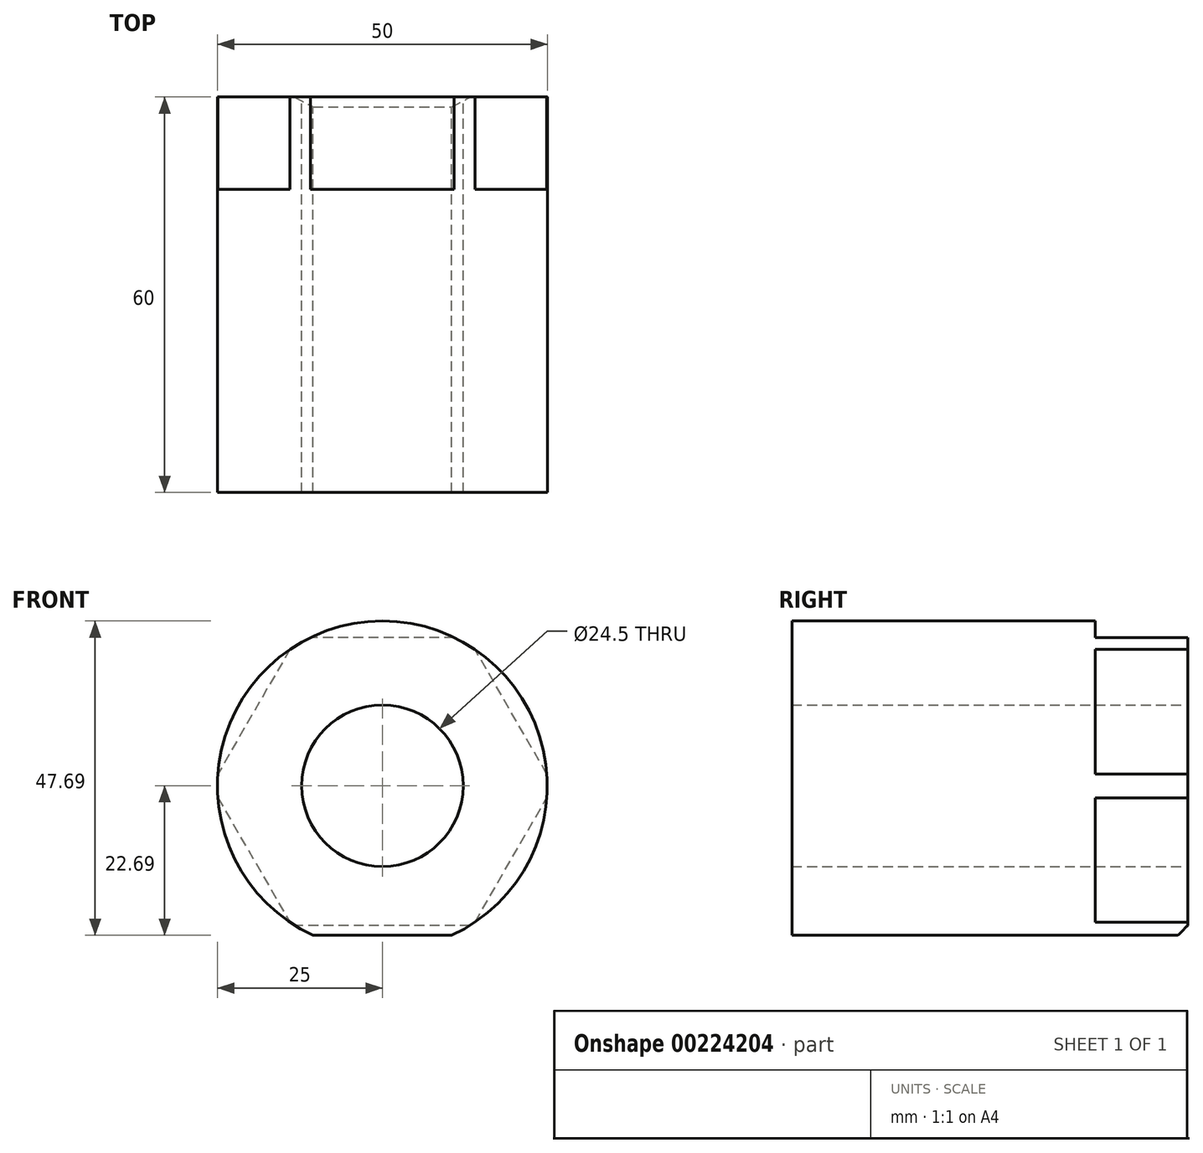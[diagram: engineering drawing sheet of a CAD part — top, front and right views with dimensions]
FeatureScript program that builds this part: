
annotation { "Feature Type Name" : "Feature", "Feature Type Description" : "" }
export const myFeature = defineFeature(function(context is Context, id is Id, definition is map)
    precondition{}
    {
        {
            var Q0;
            Q0=qCreatedBy(makeId("Front.planeOp"),FACE);
            var sketch = newSketch(context, id + "F0", { "sketchPlane" : qUnion([Q0])});
            skArc(sketch, "E0", {"start": v(10.5, -22.69) * mm, "mid": v(0, 25) * mm, "end": v(-10.5, -22.69) * mm});
            skLineSegment(sketch, "E1", {"start": v(-10.5, -22.69) * mm, "end": v(10.5, -22.69) * mm});
            skSolve(sketch);
        }
        {
            var Q0;
            Q0 = qSketchRegion(id + "F0", true);
            extrude(context, id + "F1", {"entities" : qUnion([Q0]), "depth" : 60 * mm});
        }
        {
            var Q0;
            Q0=makeQuery(id+"F1.opExtrude","CAP_FACE",FACE,{"disambiguationData":[OSD([sQuery(id+"F0.wireOp",EDGE,"E0"),sQuery(id+"F0.wireOp",EDGE,"E1")])],"isStart":true});
            var sketch = newSketch(context, id + "F2", { "sketchPlane" : qUnion([Q0])});
            skCircle(sketch, "E2.cCircle", {"center": v(0, 0) * mm, "radius": 22.5 * mm, "construction": true});
            skLineSegment(sketch, "E2.0", {"start": v(25.98, 0) * mm, "end": v(13, -22.5) * mm});
            skLineSegment(sketch, "E2.1", {"start": v(13, -22.5) * mm, "end": v(-13, -22.5) * mm});
            skLineSegment(sketch, "E2.2", {"start": v(-13, -22.5) * mm, "end": v(-25.98, 0) * mm});
            skLineSegment(sketch, "E2.3", {"start": v(-25.98, 0) * mm, "end": v(-13, 22.5) * mm});
            skLineSegment(sketch, "E2.4", {"start": v(-13, 22.5) * mm, "end": v(13, 22.5) * mm});
            skLineSegment(sketch, "E2.5", {"start": v(13, 22.5) * mm, "end": v(25.98, 0) * mm});
            skPoint(sketch, "E2.0.midPoint", {"position": v(19.49, -11.25) * mm});
            skSolve(sketch);
        }
        {
            var Q0;
            {var subQ0=sQuery(id+"F2.wireOp",EDGE,"E2.2");var subQ1=makeQuery(id+"F1.opExtrude","CAP_EDGE",EDGE,{"disambiguationData":[OSD([sQuery(id+"F0.wireOp",EDGE,"E0")])],"isStart":true});var subQ2=makeQuery(id+"F2.imprint","INTERSECT",VERTEX,{"disambiguationData":[OD(0.0)],"derivedFrom":[subQ1,subQ0]});Q0=makeQuery(id+"F2.imprint","IMPRINT",FACE,{"disambiguationData":[TD([[makeQuery(id+"F2.imprint","IMPRINT",EDGE,{"disambiguationData":[TD([[subQ2,-1.0]])],"derivedFrom":subQ0}),1.0]])]});}
            var Q1;
            {var subQ0=sQuery(id+"F2.wireOp",EDGE,"E2.3");var subQ1=makeQuery(id+"F1.opExtrude","CAP_EDGE",EDGE,{"disambiguationData":[OSD([sQuery(id+"F0.wireOp",EDGE,"E0")])],"isStart":true});var subQ2=makeQuery(id+"F2.imprint","INTERSECT",VERTEX,{"disambiguationData":[OD(0.0)],"derivedFrom":[subQ1,subQ0]});Q1=makeQuery(id+"F2.imprint","IMPRINT",FACE,{"disambiguationData":[TD([[makeQuery(id+"F2.imprint","IMPRINT",EDGE,{"disambiguationData":[TD([[subQ2,-1.0]])],"derivedFrom":subQ0}),1.0]])]});}
            var Q2;
            {var subQ0=sQuery(id+"F2.wireOp",EDGE,"E2.4");var subQ1=makeQuery(id+"F1.opExtrude","CAP_EDGE",EDGE,{"disambiguationData":[OSD([sQuery(id+"F0.wireOp",EDGE,"E0")])],"isStart":true});var subQ2=makeQuery(id+"F2.imprint","INTERSECT",VERTEX,{"disambiguationData":[OD(0.0)],"derivedFrom":[subQ1,subQ0]});Q2=makeQuery(id+"F2.imprint","IMPRINT",FACE,{"disambiguationData":[TD([[makeQuery(id+"F2.imprint","IMPRINT",EDGE,{"disambiguationData":[TD([[subQ2,-1.0]])],"derivedFrom":subQ0}),1.0]])]});}
            var Q3;
            {var subQ0=sQuery(id+"F2.wireOp",EDGE,"E2.0");var subQ1=makeQuery(id+"F1.opExtrude","CAP_EDGE",EDGE,{"disambiguationData":[OSD([sQuery(id+"F0.wireOp",EDGE,"E0")])],"isStart":true});var subQ2=makeQuery(id+"F2.imprint","INTERSECT",VERTEX,{"disambiguationData":[OD(0.0)],"derivedFrom":[subQ1,subQ0]});Q3=makeQuery(id+"F2.imprint","IMPRINT",FACE,{"disambiguationData":[TD([[makeQuery(id+"F2.imprint","IMPRINT",EDGE,{"disambiguationData":[TD([[subQ2,-1.0]])],"derivedFrom":subQ0}),1.0]])]});}
            var Q4;
            {var subQ0=sQuery(id+"F2.wireOp",EDGE,"E2.5");var subQ1=makeQuery(id+"F1.opExtrude","CAP_EDGE",EDGE,{"disambiguationData":[OSD([sQuery(id+"F0.wireOp",EDGE,"E0")])],"isStart":true});var subQ2=makeQuery(id+"F2.imprint","INTERSECT",VERTEX,{"disambiguationData":[OD(0.0)],"derivedFrom":[subQ1,subQ0]});Q4=makeQuery(id+"F2.imprint","IMPRINT",FACE,{"disambiguationData":[TD([[makeQuery(id+"F2.imprint","IMPRINT",EDGE,{"disambiguationData":[TD([[subQ2,-1.0]])],"derivedFrom":subQ0}),1.0]])]});}
            extrude(context, id + "F3", {"entities" : qUnion([Q0, Q1, Q2, Q3, Q4]), "operationType" : NewBodyOperationType.REMOVE, "oppositeDirection" : true, "depth" : 14 * mm});
        }
        {
            var Q0;
            Q0=sQuery(id+"F2.wireOp",VERTEX,"E2.cCircle.center");
            var Q1;
            Q1=makeQuery(id+"F1.opExtrude","SWEPT_BODY",BODY,{"disambiguationData":[OSD([sQuery(id+"F0.wireOp",EDGE,"E0"),sQuery(id+"F0.wireOp",EDGE,"E1")])]});
            hole(context, id + "F4", {"style" : HoleStyle.SIMPLE, "endStyle" : HoleEndStyle.THROUGH, "holeDiameter" : 24.5 * mm, "locations" : qUnion([Q0]), "scope" : qUnion([Q1]), "isTappedThrough" : true});
        }
        {
            var Q0;
            Q0=makeQuery(id+"F3.boolean.opBoolean","COPY",EDGE,{"derivedFrom":makeQuery(id+"F3.opExtrude","CAP_EDGE",EDGE,{"disambiguationData":[OSD([sQuery(id+"F2.wireOp",EDGE,"E2.2")])],"isStart":true})});
            var Q1;
            Q1=makeQuery(id+"F1.opExtrude","CAP_EDGE",EDGE,{"disambiguationData":[OSD([sQuery(id+"F0.wireOp",EDGE,"E1")])],"isStart":true});
            var Q2;
            Q2=makeQuery(id+"F3.boolean.opBoolean","COPY",EDGE,{"derivedFrom":makeQuery(id+"F3.opExtrude","CAP_EDGE",EDGE,{"disambiguationData":[OSD([sQuery(id+"F2.wireOp",EDGE,"E2.0")])],"isStart":true})});
            var Q3;
            Q3=makeQuery(id+"F3.boolean.opBoolean","COPY",EDGE,{"derivedFrom":makeQuery(id+"F3.opExtrude","CAP_EDGE",EDGE,{"disambiguationData":[OSD([sQuery(id+"F2.wireOp",EDGE,"E2.5")])],"isStart":true})});
            var Q4;
            Q4=makeQuery(id+"F3.boolean.opBoolean","COPY",EDGE,{"derivedFrom":makeQuery(id+"F3.opExtrude","CAP_EDGE",EDGE,{"disambiguationData":[OSD([sQuery(id+"F2.wireOp",EDGE,"E2.4")])],"isStart":true})});
            var Q5;
            Q5=makeQuery(id+"F3.boolean.opBoolean","COPY",EDGE,{"derivedFrom":makeQuery(id+"F3.opExtrude","CAP_EDGE",EDGE,{"disambiguationData":[OSD([sQuery(id+"F2.wireOp",EDGE,"E2.3")])],"isStart":true})});
            chamfer(context, id + "F5", {"entities" : qUnion([Q0, Q1, Q2, Q3, Q4, Q5]), "chamferType" : ChamferType.OFFSET_ANGLE, "width" : 1.5 * mm, "oppositeDirection" : false, "angle" : 45 * degree, "tangentPropagation" : true});
        }
    });
